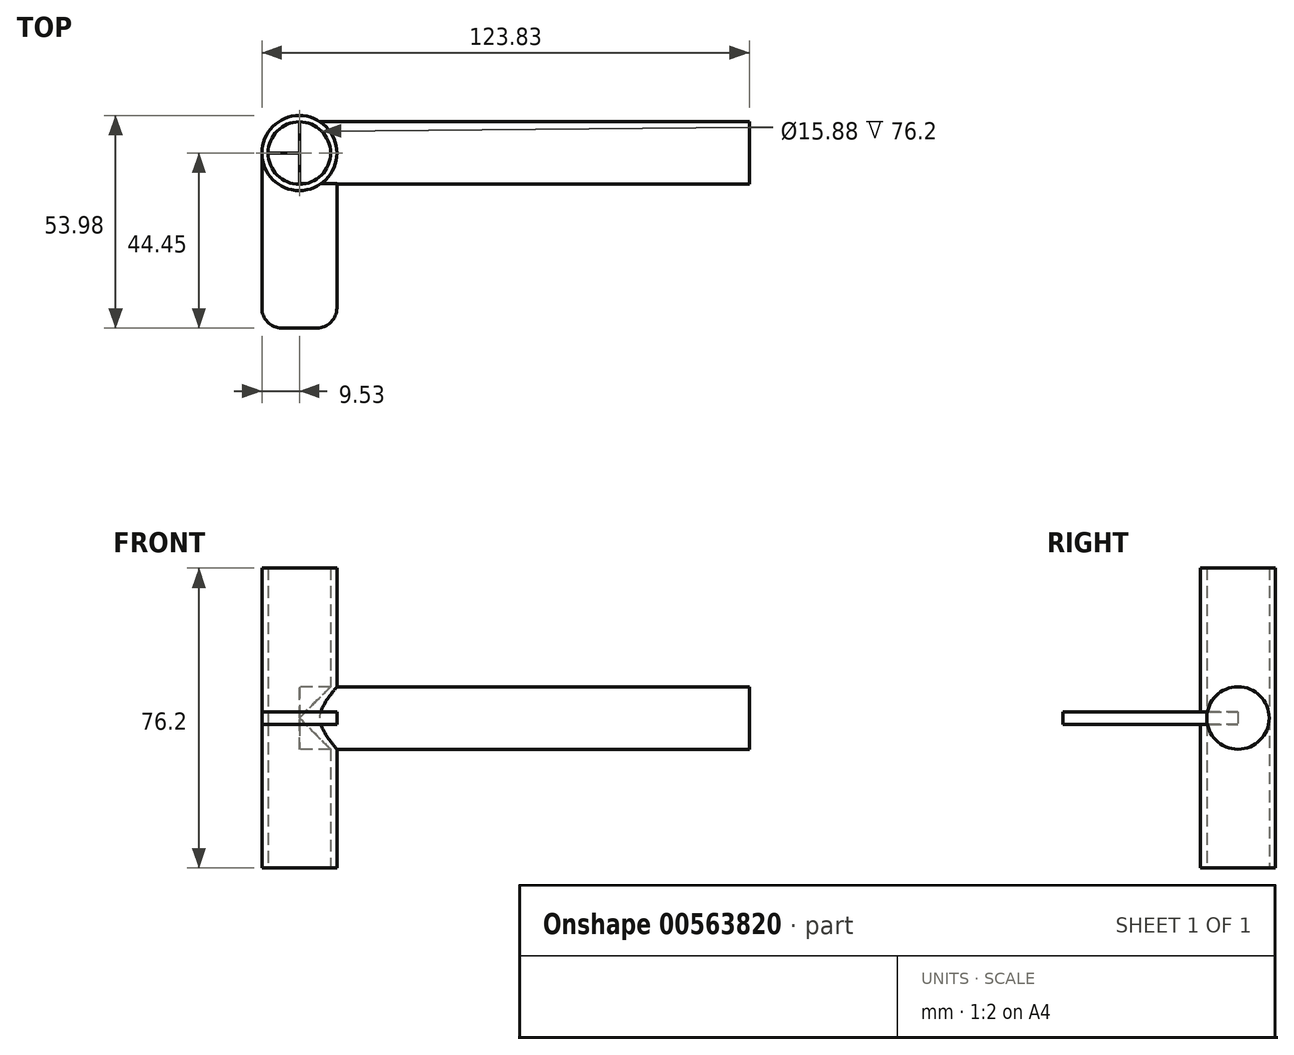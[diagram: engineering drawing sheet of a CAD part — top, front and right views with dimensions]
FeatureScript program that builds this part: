
annotation { "Feature Type Name" : "Feature", "Feature Type Description" : "" }
export const myFeature = defineFeature(function(context is Context, id is Id, definition is map)
    precondition{}
    {
        {
            var Q0;
            Q0=qCreatedBy(makeId("Top.planeOp"),FACE);
            var sketch = newSketch(context, id + "F0", { "sketchPlane" : qUnion([Q0])});
            skCircle(sketch, "E0", {"center": v(0, 0) * mm, "radius": 9.53 * mm});
            skCircle(sketch, "E1", {"center": v(0, 0) * mm, "radius": 7.94 * mm});
            skSolve(sketch);
        }
        {
            var Q0;
            Q0=makeQuery(id+"F0.imprint","IMPRINT",FACE,{"disambiguationData":[TD([[makeQuery(id+"F0.imprint","IMPRINT",EDGE,{"derivedFrom":sQuery(id+"F0.wireOp",EDGE,"E0")}),1.0]])]});
            extrude(context, id + "F1", {"entities" : qUnion([Q0]), "endBound" : BoundingType.SYMMETRIC, "depth" : 76.2 * mm, "offsetDistance" : 25.4 * mm});
        }
        {
            var Q0;
            Q0=qCreatedBy(makeId("Right.planeOp"),FACE);
            var sketch = newSketch(context, id + "F2", { "sketchPlane" : qUnion([Q0])});
            skCircle(sketch, "E2", {"center": v(0, 0) * mm, "radius": 7.94 * mm});
            skSolve(sketch);
        }
        {
            var Q0;
            Q0 = qSketchRegion(id + "F2", true);
            extrude(context, id + "F3", {"entities" : qUnion([Q0]), "operationType" : NewBodyOperationType.ADD, "depth" : 114.3 * mm, "offsetDistance" : 25.4 * mm});
        }
        {
            var Q0;
            Q0=qCreatedBy(makeId("Front.planeOp"),FACE);
            var sketch = newSketch(context, id + "F4", { "sketchPlane" : qUnion([Q0])});
            skLineSegment(sketch, "E3.bottom", {"start": v(-9.53, 1.59) * mm, "end": v(9.53, 1.59) * mm});
            skLineSegment(sketch, "E3.top", {"start": v(-9.53, -1.59) * mm, "end": v(9.53, -1.59) * mm});
            skLineSegment(sketch, "E3.left", {"start": v(-9.53, 1.59) * mm, "end": v(-9.53, -1.59) * mm});
            skLineSegment(sketch, "E3.right", {"start": v(9.53, 1.59) * mm, "end": v(9.53, -1.59) * mm});
            skPoint(sketch, "E3.middle", {"position": v(0, 0) * mm});
            skSolve(sketch);
        }
        {
            var Q0;
            Q0 = qSketchRegion(id + "F4", true);
            extrude(context, id + "F5", {"entities" : qUnion([Q0]), "operationType" : NewBodyOperationType.ADD, "depth" : 44.45 * mm, "offsetDistance" : 25.4 * mm});
        }
        {
            var Q0;
            Q0=makeQuery(id+"F5.opExtrude","CAP_EDGE",EDGE,{"disambiguationData":[OSD([sQuery(id+"F4.wireOp",EDGE,"E3.left")])],"isStart":false});
            var Q1;
            Q1=makeQuery(id+"F5.opExtrude","CAP_EDGE",EDGE,{"disambiguationData":[OSD([sQuery(id+"F4.wireOp",EDGE,"E3.right")])],"isStart":false});
            fillet(context, id + "F6", {"entities" : qUnion([Q0, Q1]), "radius" : 5.08 * mm, "tangentPropagation" : true, "allowEdgeOverflow" : false});
        }
    });
